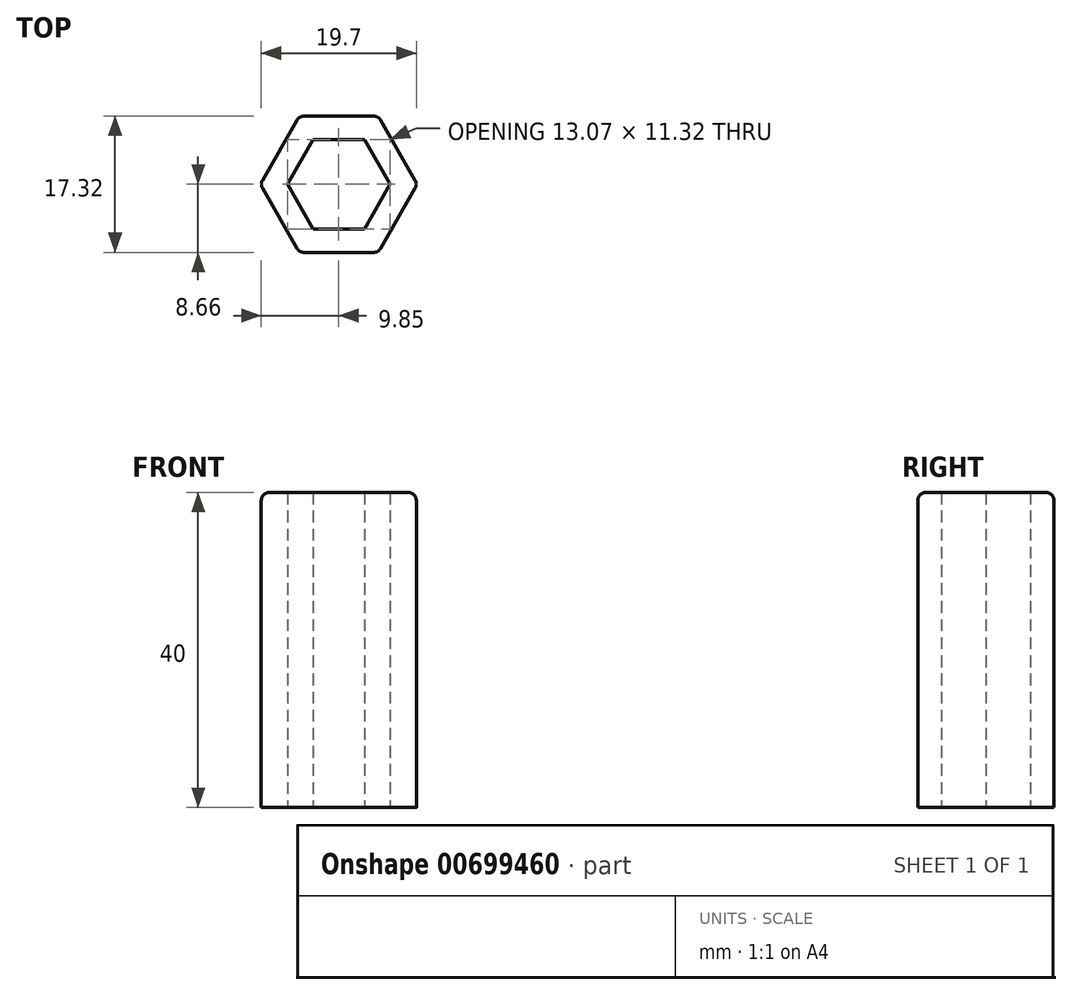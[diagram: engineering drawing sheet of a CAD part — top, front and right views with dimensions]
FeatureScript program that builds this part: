
annotation { "Feature Type Name" : "Feature", "Feature Type Description" : "" }
export const myFeature = defineFeature(function(context is Context, id is Id, definition is map)
    precondition{}
    {
        {
            var Q0;
            Q0=qCreatedBy(makeId("Top.planeOp"),FACE);
            var sketch = newSketch(context, id + "F0", { "sketchPlane" : qUnion([Q0])});
            skLineSegment(sketch, "E0.bottom", {"start": v(10, 10) * mm, "end": v(-10, 10) * mm, "construction": true});
            skLineSegment(sketch, "E0.top", {"start": v(10, -10) * mm, "end": v(-10, -10) * mm, "construction": true});
            skLineSegment(sketch, "E0.left", {"start": v(10, 10) * mm, "end": v(10, -10) * mm, "construction": true});
            skLineSegment(sketch, "E0.right", {"start": v(-10, 10) * mm, "end": v(-10, -10) * mm, "construction": true});
            skPoint(sketch, "E0.middle", {"position": v(0, 0) * mm});
            skCircle(sketch, "E1.cCircle", {"center": v(0, 0) * mm, "radius": 8.66 * mm, "construction": true});
            skLineSegment(sketch, "E1.0", {"start": v(5, 8.66) * mm, "end": v(10, 0) * mm});
            skLineSegment(sketch, "E1.1", {"start": v(10, 0) * mm, "end": v(5, -8.66) * mm});
            skLineSegment(sketch, "E1.2", {"start": v(5, -8.66) * mm, "end": v(-5, -8.66) * mm});
            skLineSegment(sketch, "E1.3", {"start": v(-5, -8.66) * mm, "end": v(-10, 0) * mm});
            skLineSegment(sketch, "E1.4", {"start": v(-10, 0) * mm, "end": v(-5, 8.66) * mm});
            skLineSegment(sketch, "E1.5", {"start": v(-5, 8.66) * mm, "end": v(5, 8.66) * mm});
            skPoint(sketch, "E1.0.midPoint", {"position": v(7.5, 4.33) * mm});
            skLineSegment(sketch, "E2.0", {"start": v(-3.27, -5.66) * mm, "end": v(-6.54, 0) * mm});
            skLineSegment(sketch, "E2.1", {"start": v(-3.27, 5.66) * mm, "end": v(3.27, 5.66) * mm});
            skLineSegment(sketch, "E2.2", {"start": v(3.27, 5.66) * mm, "end": v(6.54, 0) * mm});
            skLineSegment(sketch, "E2.3", {"start": v(-6.54, 0) * mm, "end": v(-3.27, 5.66) * mm});
            skLineSegment(sketch, "E2.4", {"start": v(6.54, 0) * mm, "end": v(3.27, -5.66) * mm});
            skLineSegment(sketch, "E2.5", {"start": v(3.27, -5.66) * mm, "end": v(-3.27, -5.66) * mm});
            skSolve(sketch);
        }
        {
            var Q0;
            Q0=qSketchRegion(id+"F0",true);
            extrude(context, id + "F1", {"entities" : qUnion([Q0]), "depth" : 40 * mm, "offsetDistance" : 25 * mm});
        }
        {
            var Q0;
            Q0=makeQuery(id+"F1.opExtrude","SWEPT_EDGE",EDGE,{"disambiguationData":[OSD([sQuery(id+"F0.wireOp",EDGE,"E1.1"),sQuery(id+"F0.wireOp",EDGE,"E1.2")])]});
            var Q1;
            Q1=makeQuery(id+"F1.opExtrude","SWEPT_EDGE",EDGE,{"disambiguationData":[OSD([sQuery(id+"F0.wireOp",EDGE,"E1.2"),sQuery(id+"F0.wireOp",EDGE,"E1.3")])]});
            var Q2;
            Q2=makeQuery(id+"F1.opExtrude","SWEPT_EDGE",EDGE,{"disambiguationData":[OSD([sQuery(id+"F0.wireOp",EDGE,"E1.0"),sQuery(id+"F0.wireOp",EDGE,"E1.1")])]});
            var Q3;
            Q3=makeQuery(id+"F1.opExtrude","SWEPT_EDGE",EDGE,{"disambiguationData":[OSD([sQuery(id+"F0.wireOp",EDGE,"E1.0"),sQuery(id+"F0.wireOp",EDGE,"E1.5")])]});
            var Q4;
            Q4=makeQuery(id+"F1.opExtrude","SWEPT_EDGE",EDGE,{"disambiguationData":[OSD([sQuery(id+"F0.wireOp",EDGE,"E1.3"),sQuery(id+"F0.wireOp",EDGE,"E1.4")])]});
            var Q5;
            Q5=makeQuery(id+"F1.opExtrude","SWEPT_EDGE",EDGE,{"disambiguationData":[OSD([sQuery(id+"F0.wireOp",EDGE,"E1.4"),sQuery(id+"F0.wireOp",EDGE,"E1.5")])]});
            var Q6;
            Q6=makeQuery(id+"F1.opExtrude","CAP_EDGE",EDGE,{"disambiguationData":[OSD([sQuery(id+"F0.wireOp",EDGE,"E1.2")])],"isStart":false});
            var Q7;
            Q7=makeQuery(id+"F1.opExtrude","CAP_EDGE",EDGE,{"disambiguationData":[OSD([sQuery(id+"F0.wireOp",EDGE,"E1.3")])],"isStart":false});
            var Q8;
            Q8=makeQuery(id+"F1.opExtrude","CAP_EDGE",EDGE,{"disambiguationData":[OSD([sQuery(id+"F0.wireOp",EDGE,"E1.4")])],"isStart":false});
            var Q9;
            Q9=makeQuery(id+"F1.opExtrude","CAP_EDGE",EDGE,{"disambiguationData":[OSD([sQuery(id+"F0.wireOp",EDGE,"E1.5")])],"isStart":false});
            var Q10;
            Q10=makeQuery(id+"F1.opExtrude","CAP_EDGE",EDGE,{"disambiguationData":[OSD([sQuery(id+"F0.wireOp",EDGE,"E1.0")])],"isStart":false});
            var Q11;
            Q11=makeQuery(id+"F1.opExtrude","CAP_EDGE",EDGE,{"disambiguationData":[OSD([sQuery(id+"F0.wireOp",EDGE,"E1.1")])],"isStart":false});
            fillet(context, id + "F2", {"entities" : qUnion([Q0, Q1, Q2, Q3, Q4, Q5, Q6, Q7, Q8, Q9, Q10, Q11]), "radius" : 1 * mm, "tangentPropagation" : true, "allowEdgeOverflow" : false});
        }
    });
